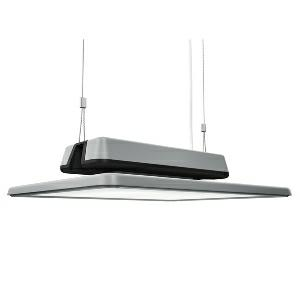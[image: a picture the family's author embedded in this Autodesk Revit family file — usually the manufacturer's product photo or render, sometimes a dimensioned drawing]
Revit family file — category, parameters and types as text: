
# Revit family: acaneo_-_hial_37000_850_w_dali_00804840_29dc
name_source: partatom
category: Lighting Fixtures
units: mm (PartAtom-declared; Revit-internal decimal feet)

## family parameters
Cut with Voids When Loaded = No
Host = Face
Light Source = No
Part Type = Normal
Room Calculation Point = No
Round Connector Dimension = Use Diameter
Shared = No

## types (1)
- ACANEO - HIAL 37000/850/W/DALI (1 x LED, 40000 lm, 5000K)
    Apparent Load = 262 VA
    Approval mark = CE
    CIE Flux Codes = 76 97 99 100 100
    Color Rendering = 80-89
    Color Temperature = 5000K
    Control Gear = Electronic ballast
    Default Elevation = 1800 mm
    Description = HIAL 37000/850/W/DALI|High bay luminaire|light source: LED|work equipment: Adjustable electronic ballast, digital DALI|connected load: 220-240 V, 50/60 Hz|Power consumption: approx. 262 W|power factor: approx. 0,981|luminous flux: 40000 lm|luminous efficacy: 152 lm/W|colour temperature: Cold white, ca. 5000 K|color rendering index (CRI): >= 80|chromaticity tolerance:  3 SDCM|System of protection: IP 65|class of protection: I|technology: Continuously dimmable|luminaire body|material: Aluminium|surface: Powder coatet|colour: White aluminium|lamp cover: Acrylic (PMMA), Clear|weight (net): approx. 10.8 kg|mains lead: Built-in plug RST 20i5 Einbau|Fastening: Available separately|Accessory: Junction box (RST 20i5)|minimum ambient temperature: -30 ░C|maximum ambient temperature: 50 ░C|glare control: Optics|unified glare rating(4H 8H): <=  25|
    Frequency = 50 Hz, 60 Hz
    Height = 125 mm
    Lamp = 1 x LED
    Lamp Light Flux = 40000 lm
    Lamp count = 1
    Length = 585 mm
    Luminous efficacy = 153 lm/W
    Manufacturer = Waldmann
    ModVariant = No
    Model = 00804840
    Mounting Place = Ceiling
    Mounting Type = Pendant
    Number of Poles = 1
    OnlyDefault = Yes
    Power Factor = 1
    Product Name = ACANEO - HIAL 37000/850/W/DALI
    Product group = High bay luminaire (industry)
    ProductGroupID = 901
    Protection Class = Protection class I
    Protection Degree = IP 65
    RLX_Detail_Level = 1
    RLX_Emergency_Light_Flux = 0 lm
    RLX_Emergency_Type = 0
    RLX_Emergency_Type_DB = No
    RlxData = <blob elided: 29965 chars, md5=41a03c3b>
    Socket = socket
    Standby Power = 0 W
    System Light Flux = 40000 lm
    System Power = 262 W
    Type Comments = Product without accessories
    Type Image = acaneo-hial.jpg
    URL = http://relux.com
    VarID = ---
    Voltage = 230 V
    Voltage Range = 110-120 V, 220-240 V
    Weight = 0.00 kg
    Width = 480 mm

## geometry (parser evidence)
native form markers: Blend x4, Sweep x9
no freeform markers — native parametric forms only
